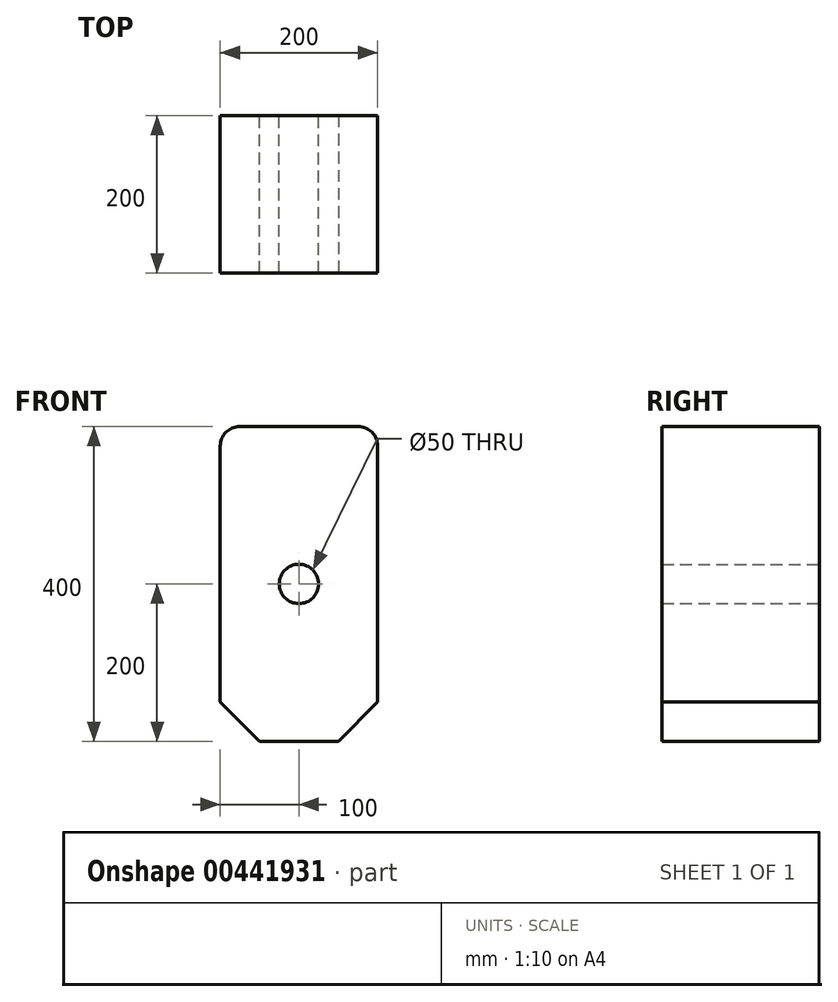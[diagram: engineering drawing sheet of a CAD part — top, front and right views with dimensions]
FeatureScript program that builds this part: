
annotation { "Feature Type Name" : "Feature", "Feature Type Description" : "" }
export const myFeature = defineFeature(function(context is Context, id is Id, definition is map)
    precondition{}
    {
        {
            var Q0;
            Q0=qCreatedBy(makeId("Front.planeOp"),FACE);
            var sketch = newSketch(context, id + "F0", { "sketchPlane" : qUnion([Q0])});
            skLineSegment(sketch, "E0.bottom", {"start": v(75, 200) * mm, "end": v(-75, 200) * mm});
            skLineSegment(sketch, "E0.top", {"start": v(100, -200) * mm, "end": v(-100, -200) * mm});
            skLineSegment(sketch, "E0.left", {"start": v(100, 175) * mm, "end": v(100, -200) * mm});
            skLineSegment(sketch, "E0.right", {"start": v(-100, 175) * mm, "end": v(-100, -200) * mm});
            skPoint(sketch, "E0.middle", {"position": v(0, 0) * mm});
            skPoint(sketch, "E1.visualSharp", {"position": v(-100, 200) * mm});
            skArc(sketch, "E1.filletArc", {"start": v(-75, 200) * mm, "mid": v(-92.68, 192.68) * mm, "end": v(-100, 175) * mm});
            skPoint(sketch, "E2.visualSharp", {"position": v(100, 200) * mm});
            skArc(sketch, "E2.filletArc", {"start": v(100, 175) * mm, "mid": v(92.68, 192.68) * mm, "end": v(75, 200) * mm});
            skCircle(sketch, "E3", {"center": v(0, 0) * mm, "radius": 25 * mm});
            skSolve(sketch);
        }
        {
            var Q0;
            Q0 = qSketchRegion(id + "F0", true);
            extrude(context, id + "F1", {"entities" : qUnion([Q0]), "depth" : 200 * mm});
        }
        {
            var Q0;
            Q0=makeQuery(id+"F1.opExtrude","SWEPT_EDGE",EDGE,{"disambiguationData":[OSD([sQuery(id+"F0.wireOp",EDGE,"E0.top"),sQuery(id+"F0.wireOp",EDGE,"E0.left")])]});
            var Q1;
            Q1=makeQuery(id+"F1.opExtrude","SWEPT_EDGE",EDGE,{"disambiguationData":[OSD([sQuery(id+"F0.wireOp",EDGE,"E0.top"),sQuery(id+"F0.wireOp",EDGE,"E0.right")])]});
            chamfer(context, id + "F2", {"entities" : qUnion([Q0, Q1]), "width" : 50 * mm, "tangentPropagation" : true});
        }
    });
